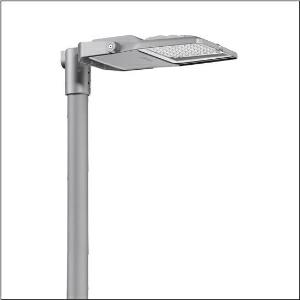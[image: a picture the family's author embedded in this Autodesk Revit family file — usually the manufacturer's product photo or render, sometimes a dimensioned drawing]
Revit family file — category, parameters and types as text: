
# Revit family: floodlight_fl_21_iq_mini___pl61_5xa7771d2c3a_41a8
name_source: partatom
category: Lighting Fixtures
units: mm (PartAtom-declared; Revit-internal decimal feet)

## family parameters
Cut with Voids When Loaded = No
Host = Face
Light Source = No
Part Type = Normal
Room Calculation Point = No
Round Connector Dimension = Use Diameter
Shared = No

## types (1)
- --- (1 x LED, 17500 lm, 143 W, 3000K)
    Apparent Load = 143 VA
    CIE Flux Codes = 33 65 98 100 100
    Color Rendering = 70
    Color Temperature = 3000K
    Default Elevation = 1800 mm
    Description = Floodlight FL 21 iQ mini, floodlight, primary light control with lens, of PMMA, primary optical cover: protective disc, of toughened safety glass, transparent, light distribution: PL61, light emission: direct distribution, installation type: surface-mounted, LED, High Power LED, rated luminous flux: 17.500lm, luminous efficacy: 122lm/W, light colour: 730, colour temperature: 3000K, control: Auto-Match, Temp-Guard, Lumen-Switch, Night-Set, Smart-Wire, Light-Fading, Desk-Remote (wireless, voltage-free reading and setting of iQ features in the workshop via application-optimized NFC function/RFID function), optimised constant luminous flux control (CLO 2.0), with terminal, 6-pole, mains connection: 220..240V, AC, 50/60Hz, start of lifetime: 143W, end of service life: 152W, reduction: 61W, luminaire housing, of diecast aluminium, powder-coated, Siteco® metallic grey (DB 702S), corrosivity category C5 mid according to DIN EN ISO 12944, sealing non-destructively replaceable, please order mast flange separately, mast bracket, of steel, galvanised, powder-coated, Siteco® metallic grey (DB 702S), protection rating (complete): IP66, insulation class (complete): insulation class II (safety insulation), certification: CE, ENEC, VDE, protection symbol: D, impact resistance: IK08, permissible operating ambient temperature: -40..+40°C, permissible operating ambient temperature for outdoor applications: -40..+50°C, standard: DIN EN 12944, LABS conformity tested according to VDMA 24364:2018-05, packaging unit: 1 piece

Light Distribution: PL61
    Height = 70 mm
    Lamp = 1 x LED
    Lamp Light Flux = 17500 lm
    Lamp Power = 143 W
    Lamp count = 1
    Length = 485 mm
    Luminous efficacy = 122 lm/W
    Manufacturer = Siteco
    ModVariant = No
    Model = 5XA7771D2C3A
    Number of Poles = 1
    OnlyDefault = Yes
    Power Factor = 1
    Product Name = Floodlight FL 21 iQ mini | PL61
    Product group = floodlight | pylon annexe
    ProductGroupID = 6200
    Protection Class = Protection class II
    Protection Degree = IP 66
    RLX_Detail_Level = 1
    RLX_Emergency_Light_Flux = 0 lm
    RLX_Emergency_Type = 0
    RLX_Emergency_Type_DB = No
    RlxData = <blob elided: 101621 chars, md5=8c2b475d>
    Socket = socket
    Standby Power = 0 W
    System Light Flux = 17500 lm
    System Power = 143 W
    Type Comments = factory setting: luminous flux: 100 % | dim-lin: 254 | 730 mA
    Type Image = l_1007125.jpg
    URL = http://relux.com
    VarID = @adj_105793
    Voltage = 0 V
    Weight = 0.00 kg
    Width = 337 mm

## geometry (parser evidence)
native form markers: Blend x4, Sweep x10
no freeform markers — native parametric forms only
